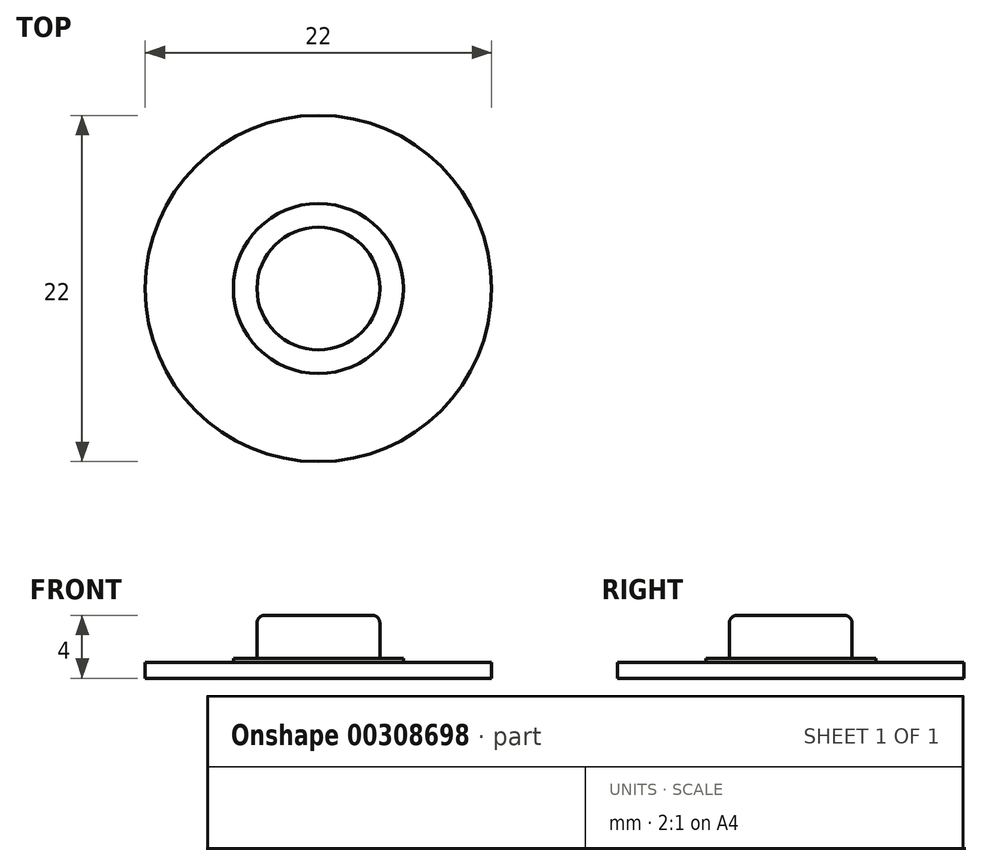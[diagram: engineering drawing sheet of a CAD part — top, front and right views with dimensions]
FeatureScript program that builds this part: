
annotation { "Feature Type Name" : "Feature", "Feature Type Description" : "" }
export const myFeature = defineFeature(function(context is Context, id is Id, definition is map)
    precondition{}
    {
        {
            assignVariable(context, id + "F0", {"name" : "Depth", "anyValue" : 6 * mm});
        }
        {
            assignVariable(context, id + "F1", {"name" : "CapHeight", "anyValue" : 1 * mm});
        }
        {
            var Q0;
            Q0=qCreatedBy(makeId("Top.planeOp"),FACE);
            var sketch = newSketch(context, id + "F2", { "sketchPlane" : qUnion([Q0])});
            skCircle(sketch, "E0", {"center": v(0, 0) * mm, "radius": 11 * mm});
            skCircle(sketch, "E1", {"center": v(0, 0) * mm, "radius": 3.9 * mm});
            skCircle(sketch, "E2", {"center": v(0, 0) * mm, "radius": 5.4 * mm});
            skSolve(sketch);
        }
        {
            var Q0;
            Q0=makeQuery(id+"F2.imprint","IMPRINT",FACE,{"disambiguationData":[TD([[makeQuery(id+"F2.imprint","IMPRINT",EDGE,{"derivedFrom":sQuery(id+"F2.wireOp",EDGE,"E0")}),1.0]])]});
            var Q1;
            {var subQ0=sQuery(id+"F2.wireOp",EDGE,"Aik3Fh94-IEyG-y0ab-I86t-QxJy3uRAjjuj");var subQ1=sQuery(id+"F2.wireOp",EDGE,"eddf496a-69cb-4dca-af1a-5cfb339baa00.cCircle");var subQ2=makeQuery(id+"F2.imprint","INTERSECT",VERTEX,{"derivedFrom":[subQ1,subQ0]});Q1=makeQuery(id+"F2.imprint","IMPRINT",FACE,{"disambiguationData":[TD([[makeQuery(id+"F2.imprint","IMPRINT",EDGE,{"disambiguationData":[TD([[subQ2,-1.0]])],"derivedFrom":subQ1}),1.0]])]});}
            var Q2;
            {var subQ0=sQuery(id+"F2.wireOp",EDGE,"bQPTAbcu-4Vbk-pjXa-VLoq-6PIaxohuaGXJ");var subQ1=sQuery(id+"F2.wireOp",EDGE,"E1");var subQ2=makeQuery(id+"F2.imprint","INTERSECT",VERTEX,{"derivedFrom":[subQ1,subQ0]});Q2=makeQuery(id+"F2.imprint","IMPRINT",FACE,{"disambiguationData":[TD([[makeQuery(id+"F2.imprint","IMPRINT",EDGE,{"disambiguationData":[TD([[subQ2,1.0]])],"derivedFrom":subQ1}),1.0]])]});}
            var Q3;
            {var subQ0=sQuery(id+"F2.wireOp",EDGE,"RFFd7nfY-Md6k-aeHc-cift-ULqT6TmYogZ5");var subQ1=sQuery(id+"F2.wireOp",EDGE,"E1");var subQ2=makeQuery(id+"F2.imprint","INTERSECT",VERTEX,{"derivedFrom":[subQ1,subQ0]});Q3=makeQuery(id+"F2.imprint","IMPRINT",FACE,{"disambiguationData":[TD([[makeQuery(id+"F2.imprint","IMPRINT",EDGE,{"disambiguationData":[TD([[subQ2,1.0]])],"derivedFrom":subQ1}),1.0]])]});}
            var Q4;
            {var subQ0=sQuery(id+"F2.wireOp",EDGE,"Aik3Fh94-IEyG-y0ab-I86t-QxJy3uRAjjuj");var subQ1=sQuery(id+"F2.wireOp",EDGE,"E1");var subQ2=makeQuery(id+"F2.imprint","INTERSECT",VERTEX,{"derivedFrom":[subQ1,subQ0]});Q4=makeQuery(id+"F2.imprint","IMPRINT",FACE,{"disambiguationData":[TD([[makeQuery(id+"F2.imprint","IMPRINT",EDGE,{"disambiguationData":[TD([[subQ2,-1.0]])],"derivedFrom":subQ1}),1.0]])]});}
            var Q5;
            {var subQ0=sQuery(id+"F2.wireOp",EDGE,"bQPTAbcu-4Vbk-pjXa-VLoq-6PIaxohuaGXJ");var subQ1=sQuery(id+"F2.wireOp",EDGE,"eddf496a-69cb-4dca-af1a-5cfb339baa00.cCircle");var subQ2=makeQuery(id+"F2.imprint","INTERSECT",VERTEX,{"derivedFrom":[subQ1,subQ0]});Q5=makeQuery(id+"F2.imprint","IMPRINT",FACE,{"disambiguationData":[TD([[makeQuery(id+"F2.imprint","IMPRINT",EDGE,{"disambiguationData":[TD([[subQ2,1.0]])],"derivedFrom":subQ1}),1.0]])]});}
            var Q6;
            {var subQ0=sQuery(id+"F2.wireOp",EDGE,"Aik3Fh94-IEyG-y0ab-I86t-QxJy3uRAjjuj");var subQ1=sQuery(id+"F2.wireOp",EDGE,"E1");var subQ2=makeQuery(id+"F2.imprint","INTERSECT",VERTEX,{"derivedFrom":[subQ1,subQ0]});Q6=makeQuery(id+"F2.imprint","IMPRINT",FACE,{"disambiguationData":[TD([[makeQuery(id+"F2.imprint","IMPRINT",EDGE,{"disambiguationData":[TD([[subQ2,1.0]])],"derivedFrom":subQ1}),1.0]])]});}
            var Q7;
            {var subQ0=sQuery(id+"F2.wireOp",EDGE,"q5uM22f2-6PhJ-HLYM-6dBt-ZQmkEjkwKoLg");var subQ1=sQuery(id+"F2.wireOp",EDGE,"E1");var subQ2=makeQuery(id+"F2.imprint","INTERSECT",VERTEX,{"derivedFrom":[subQ1,subQ0]});Q7=makeQuery(id+"F2.imprint","IMPRINT",FACE,{"disambiguationData":[TD([[makeQuery(id+"F2.imprint","IMPRINT",EDGE,{"disambiguationData":[TD([[subQ2,1.0]])],"derivedFrom":subQ1}),1.0]])]});}
            var Q8;
            {var subQ0=sQuery(id+"F2.wireOp",EDGE,"j7NdKZBS-zRsD-m3iY-UzBS-RkiyrTsFpgP3");var subQ1=sQuery(id+"F2.wireOp",EDGE,"eddf496a-69cb-4dca-af1a-5cfb339baa00.cCircle");var subQ2=makeQuery(id+"F2.imprint","INTERSECT",VERTEX,{"derivedFrom":[subQ1,subQ0]});Q8=makeQuery(id+"F2.imprint","IMPRINT",FACE,{"disambiguationData":[TD([[makeQuery(id+"F2.imprint","IMPRINT",EDGE,{"disambiguationData":[TD([[subQ2,-1.0]])],"derivedFrom":subQ1}),1.0]])]});}
            var Q9;
            {var subQ0=sQuery(id+"F2.wireOp",EDGE,"70BWp4Ch-3ug6-KJnD-76Ve-rYQtWEBfFcAG");var subQ1=sQuery(id+"F2.wireOp",EDGE,"eddf496a-69cb-4dca-af1a-5cfb339baa00.cCircle");var subQ2=makeQuery(id+"F2.imprint","INTERSECT",VERTEX,{"derivedFrom":[subQ1,subQ0]});Q9=makeQuery(id+"F2.imprint","IMPRINT",FACE,{"disambiguationData":[TD([[makeQuery(id+"F2.imprint","IMPRINT",EDGE,{"disambiguationData":[TD([[subQ2,-1.0]])],"derivedFrom":subQ1}),1.0]])]});}
            var Q10;
            {var subQ0=sQuery(id+"F2.wireOp",EDGE,"q5uM22f2-6PhJ-HLYM-6dBt-ZQmkEjkwKoLg");var subQ1=sQuery(id+"F2.wireOp",EDGE,"eddf496a-69cb-4dca-af1a-5cfb339baa00.cCircle");var subQ2=makeQuery(id+"F2.imprint","INTERSECT",VERTEX,{"derivedFrom":[subQ1,subQ0]});Q10=makeQuery(id+"F2.imprint","IMPRINT",FACE,{"disambiguationData":[TD([[makeQuery(id+"F2.imprint","IMPRINT",EDGE,{"disambiguationData":[TD([[subQ2,-1.0]])],"derivedFrom":subQ1}),1.0]])]});}
            var Q11;
            {var subQ0=sQuery(id+"F2.wireOp",EDGE,"q5uM22f2-6PhJ-HLYM-6dBt-ZQmkEjkwKoLg");var subQ1=sQuery(id+"F2.wireOp",EDGE,"eddf496a-69cb-4dca-af1a-5cfb339baa00.cCircle");var subQ2=makeQuery(id+"F2.imprint","INTERSECT",VERTEX,{"derivedFrom":[subQ1,subQ0]});Q11=makeQuery(id+"F2.imprint","IMPRINT",FACE,{"disambiguationData":[TD([[makeQuery(id+"F2.imprint","IMPRINT",EDGE,{"disambiguationData":[TD([[subQ2,1.0]])],"derivedFrom":subQ1}),1.0]])]});}
            var Q12;
            {var subQ0=sQuery(id+"F2.wireOp",EDGE,"j7NdKZBS-zRsD-m3iY-UzBS-RkiyrTsFpgP3");var subQ1=sQuery(id+"F2.wireOp",EDGE,"E1");var subQ2=makeQuery(id+"F2.imprint","INTERSECT",VERTEX,{"derivedFrom":[subQ1,subQ0]});Q12=makeQuery(id+"F2.imprint","IMPRINT",FACE,{"disambiguationData":[TD([[makeQuery(id+"F2.imprint","IMPRINT",EDGE,{"disambiguationData":[TD([[subQ2,1.0]])],"derivedFrom":subQ1}),1.0]])]});}
            var Q13;
            Q13=makeQuery(id+"F2.imprint","IMPRINT",FACE,{"disambiguationData":[TD([[makeQuery(id+"F2.imprint","IMPRINT",EDGE,{"derivedFrom":sQuery(id+"F2.wireOp",EDGE,"E1")}),1.0]])]});
            var Q14;
            Q14=makeQuery(id+"F2.imprint","IMPRINT",FACE,{"disambiguationData":[TD([[makeQuery(id+"F2.imprint","IMPRINT",EDGE,{"derivedFrom":sQuery(id+"F2.wireOp",EDGE,"E1")}),-1.0]])]});
            extrude(context, id + "F3", {"entities" : qUnion([Q0, Q1, Q2, Q3, Q4, Q5, Q6, Q7, Q8, Q9, Q10, Q11, Q12, Q13, Q14]), "oppositeDirection" : true, "depth" : getVariable(context, 'CapHeight')});
        }
        {
            var Q0;
            Q0=makeQuery(id+"F2.imprint","IMPRINT",FACE,{"disambiguationData":[TD([[makeQuery(id+"F2.imprint","IMPRINT",EDGE,{"derivedFrom":sQuery(id+"F2.wireOp",EDGE,"E1")}),1.0]])]});
            extrude(context, id + "F4", {"entities" : qUnion([Q0]), "operationType" : NewBodyOperationType.ADD, "depth" : getVariable(context, 'Depth') / 2});
        }
        {
            var Q0;
            Q0=makeQuery(id+"F2.imprint","IMPRINT",FACE,{"disambiguationData":[TD([[makeQuery(id+"F2.imprint","IMPRINT",EDGE,{"derivedFrom":sQuery(id+"F2.wireOp",EDGE,"E1")}),-1.0]])]});
            extrude(context, id + "F5", {"entities" : qUnion([Q0]), "operationType" : NewBodyOperationType.ADD, "depth" : .25 * mm});
        }
        {
            var Q0;
            Q0=makeQuery(id+"F4.opExtrude","CAP_EDGE",EDGE,{"disambiguationData":[OSD([sQuery(id+"F2.wireOp",EDGE,"E1")])],"isStart":false});
            fillet(context, id + "F6", {"entities" : qUnion([Q0]), "radius" : .5 * mm, "tangentPropagation" : true, "allowEdgeOverflow" : false});
        }
    });
